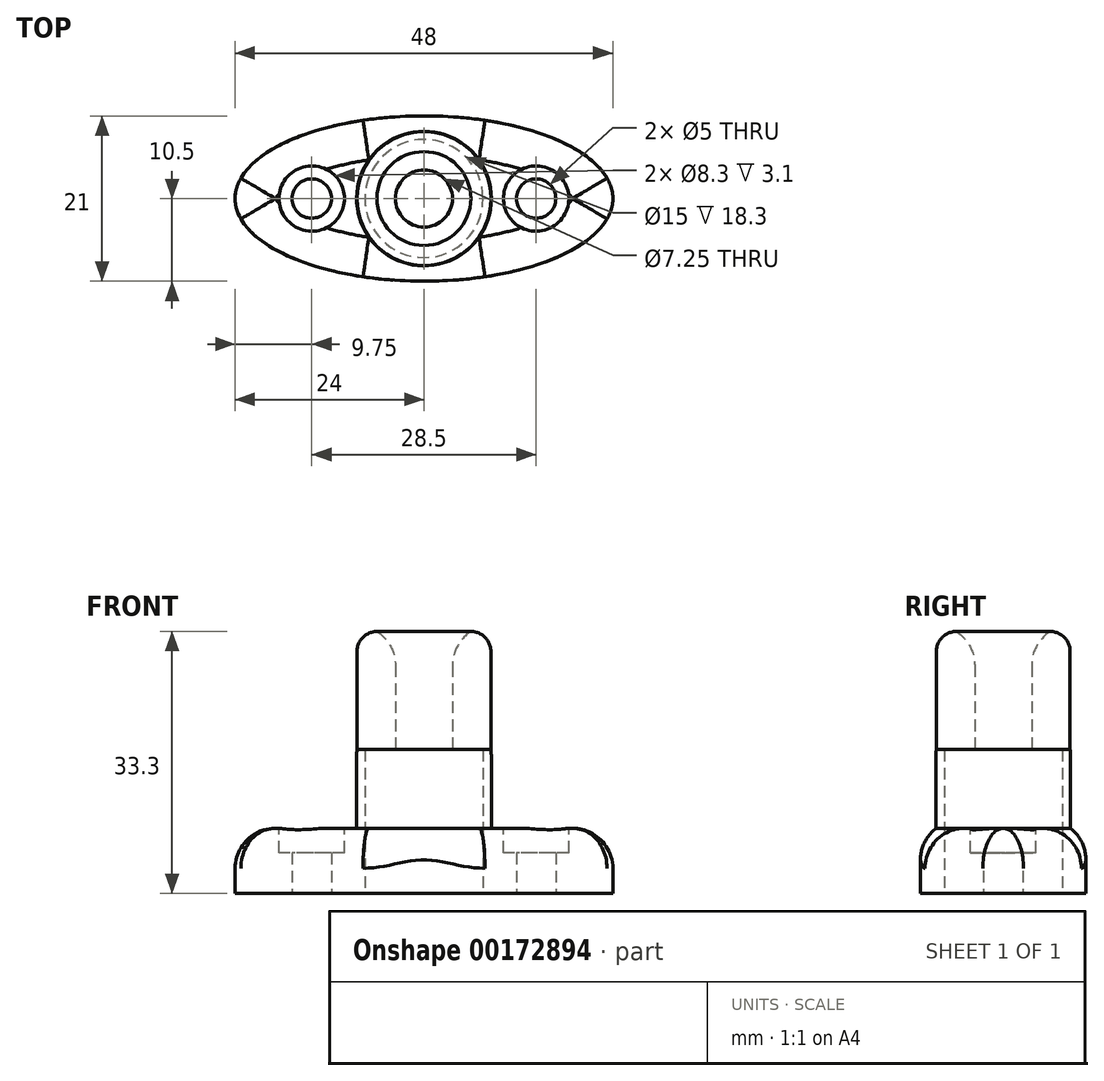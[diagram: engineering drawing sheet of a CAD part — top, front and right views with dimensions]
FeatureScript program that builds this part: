
annotation { "Feature Type Name" : "Feature", "Feature Type Description" : "" }
export const myFeature = defineFeature(function(context is Context, id is Id, definition is map)
    precondition{}
    {
        {
            var Q0;
            Q0=qCreatedBy(makeId("Top.planeOp"),FACE);
            var sketch = newSketch(context, id + "F0", { "sketchPlane" : qUnion([Q0])});
            skEllipse(sketch, "E0", {"center": v(0, 0) * mm, "majorRadius": 24 * mm, "minorRadius": 10.5 * mm, "majorAxis": v(-1, 0)});
            skLineSegment(sketch, "E1", {"start": v(-24, 0) * mm, "end": v(24, 0) * mm});
            skCircle(sketch, "E2", {"center": v(0, 0) * mm, "radius": 7.5 * mm});
            skCircle(sketch, "E3", {"center": v(14.25, 0) * mm, "radius": 2.5 * mm});
            skCircle(sketch, "E4", {"center": v(-14.25, 0) * mm, "radius": 2.5 * mm});
            skSolve(sketch);
        }
        {
            var Q0;
            Q0=makeQuery(id+"F0.imprint","IMPRINT",FACE,{"disambiguationData":[TD([[makeQuery(id+"F0.imprint","IMPRINT",EDGE,{"derivedFrom":sQuery(id+"F0.wireOp",EDGE,"E0")}),1.0]])]});
            extrude(context, id + "F1", {"entities" : qUnion([Q0]), "depth" : 8.3 * mm});
        }
        {
            var Q0;
            Q0=makeQuery(id+"F1.opExtrude","CAP_FACE",FACE,{"disambiguationData":[OSD([sQuery(id+"F0.wireOp",EDGE,"E0"),sQuery(id+"F0.wireOp",EDGE,"E2"),sQuery(id+"F0.wireOp",EDGE,"E3"),sQuery(id+"F0.wireOp",EDGE,"E4")])],"isStart":false});
            var sketch = newSketch(context, id + "F2", { "sketchPlane" : qUnion([Q0])});
            skCircle(sketch, "E5", {"center": v(0, 0) * mm, "radius": 8.55 * mm});
            skCircle(sketch, "E6", {"center": v(0, 0) * mm, "radius": 7.5 * mm});
            skCircle(sketch, "E7", {"center": v(-14.25, 0) * mm, "radius": 4.15 * mm});
            skCircle(sketch, "E8", {"center": v(14.25, 0) * mm, "radius": 4.15 * mm});
            skSolve(sketch);
        }
        {
            var Q0;
            Q0=makeQuery(id+"F2.imprint","IMPRINT",FACE,{"disambiguationData":[TD([[makeQuery(id+"F2.imprint","IMPRINT",EDGE,{"derivedFrom":sQuery(id+"F2.wireOp",EDGE,"E5")}),1.0]])]});
            extrude(context, id + "F3", {"entities" : qUnion([Q0]), "operationType" : NewBodyOperationType.ADD, "depth" : 10 * mm});
        }
        {
            var Q0;
            Q0=makeQuery(id+"F2.imprint","IMPRINT",FACE,{"disambiguationData":[TD([[makeQuery(id+"F2.imprint","IMPRINT",EDGE,{"derivedFrom":sQuery(id+"F2.wireOp",EDGE,"E7")}),1.0]])]});
            var Q1;
            Q1=makeQuery(id+"F2.imprint","IMPRINT",FACE,{"disambiguationData":[TD([[makeQuery(id+"F2.imprint","IMPRINT",EDGE,{"derivedFrom":sQuery(id+"F2.wireOp",EDGE,"E8")}),1.0]])]});
            extrude(context, id + "F4", {"entities" : qUnion([Q0, Q1]), "operationType" : NewBodyOperationType.REMOVE, "oppositeDirection" : true, "depth" : 3.1 * mm});
        }
        {
            var Q0;
            Q0=makeQuery(id+"F3.opExtrude","CAP_FACE",FACE,{"disambiguationData":[OSD([sQuery(id+"F2.wireOp",EDGE,"E5"),sQuery(id+"F2.wireOp",EDGE,"E6")])],"isStart":false});
            var sketch = newSketch(context, id + "F5", { "sketchPlane" : qUnion([Q0])});
            skCircle(sketch, "E9", {"center": v(0, 0) * mm, "radius": 8.5 * mm});
            skCircle(sketch, "E10", {"center": v(0, 0) * mm, "radius": 3.62 * mm});
            skSolve(sketch);
        }
        {
            var Q0;
            Q0=makeQuery(id+"F5.imprint","IMPRINT",FACE,{"disambiguationData":[TD([[makeQuery(id+"F5.imprint","IMPRINT",EDGE,{"derivedFrom":sQuery(id+"F5.wireOp",EDGE,"E10")}),-1.0]])]});
            var Q1;
            Q1=makeQuery(id+"F5.imprint","IMPRINT",FACE,{"disambiguationData":[TD([[makeQuery(id+"F5.imprint","IMPRINT",EDGE,{"derivedFrom":sQuery(id+"F5.wireOp",EDGE,"E9")}),1.0]])]});
            extrude(context, id + "F6", {"entities" : qUnion([Q0, Q1]), "operationType" : NewBodyOperationType.ADD, "depth" : 15 * mm});
        }
        {
            var Q0;
            Q0=makeQuery(id+"F3.opExtrude","CAP_EDGE",EDGE,{"disambiguationData":[OSD([sQuery(id+"F2.wireOp",EDGE,"E5")])],"isStart":true});
            var Q1;
            Q1=makeQuery(id+"F6.opExtrude","CAP_EDGE",EDGE,{"disambiguationData":[OSD([sQuery(id+"F5.wireOp",EDGE,"E9")])],"isStart":false});
            fillet(context, id + "F7", {"entities" : qUnion([Q0, Q1]), "radius" : 2.54 * mm, "tangentPropagation" : true, "allowEdgeOverflow" : false});
        }
        {
            var Q0;
            Q0=makeQuery(id+"F1.opExtrude","CAP_EDGE",EDGE,{"disambiguationData":[OSD([sQuery(id+"F0.wireOp",EDGE,"E0")])],"isStart":false});
            var Q1;
            Q1=makeQuery(id+"F6.opExtrude","CAP_EDGE",EDGE,{"disambiguationData":[OSD([sQuery(id+"F5.wireOp",EDGE,"E10")])],"isStart":false});
            var Q2;
            Q2=makeQuery(id+"F3.opExtrude","CAP_EDGE",EDGE,{"disambiguationData":[OSD([sQuery(id+"F2.wireOp",EDGE,"E5")])],"isStart":false});
            fillet(context, id + "F8", {"entities" : qUnion([Q0, Q1, Q2]), "radius" : 5.08 * mm, "tangentPropagation" : true, "allowEdgeOverflow" : false});
        }
    });
